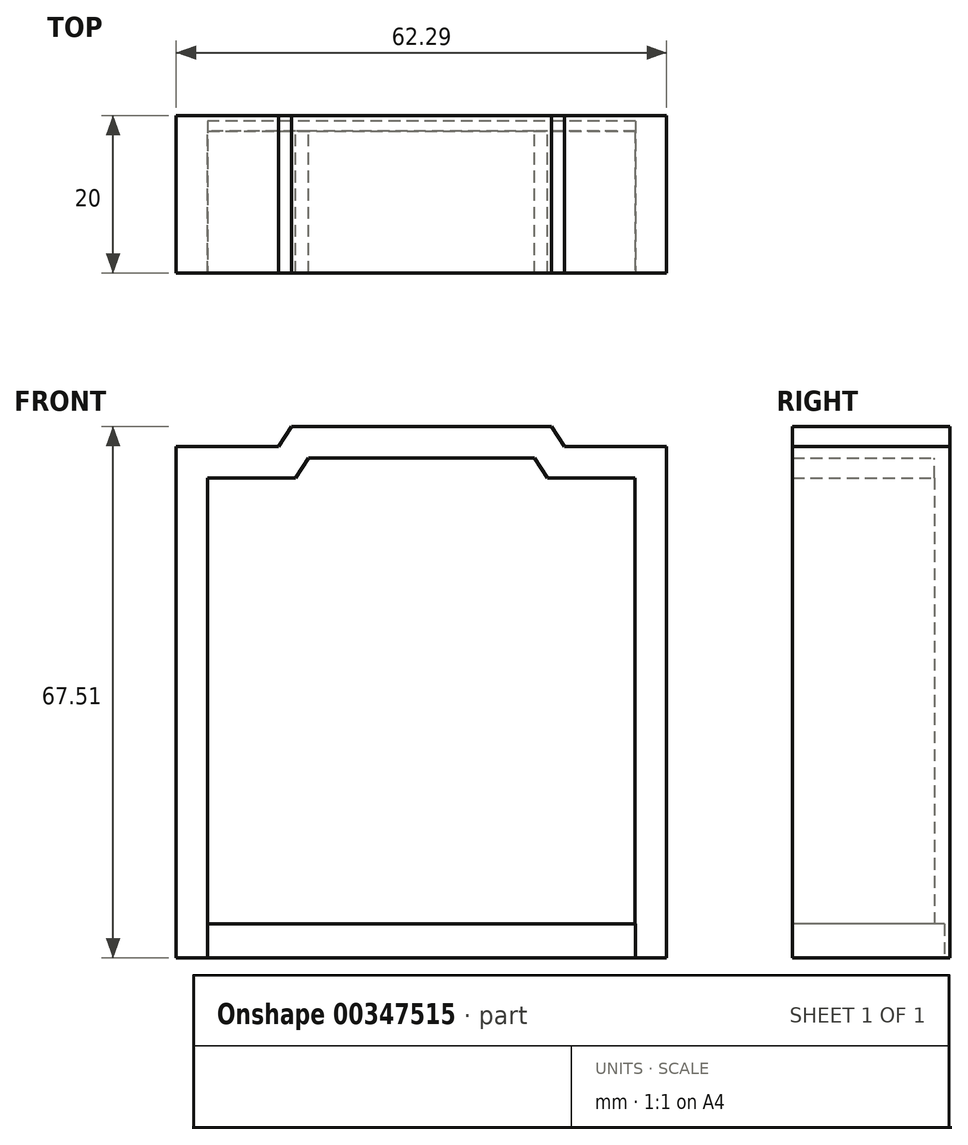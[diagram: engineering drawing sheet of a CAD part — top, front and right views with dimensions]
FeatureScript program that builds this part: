
annotation { "Feature Type Name" : "Feature", "Feature Type Description" : "" }
export const myFeature = defineFeature(function(context is Context, id is Id, definition is map)
    precondition{}
    {
        {
            var Q0;
            Q0=qCreatedBy(makeId("Front.planeOp"),FACE);
            var sketch = newSketch(context, id + "F0", { "sketchPlane" : qUnion([Q0])});
            skLineSegment(sketch, "E0", {"start": v(0, 0) * mm, "end": v(53, 0) * mm});
            skLineSegment(sketch, "E1", {"start": v(53, 0) * mm, "end": v(53, 65) * mm});
            skLineSegment(sketch, "E2", {"start": v(53, 65) * mm, "end": v(40, 65) * mm});
            skLineSegment(sketch, "E3", {"start": v(40, 65) * mm, "end": v(38.35, 67.5) * mm});
            skLineSegment(sketch, "E4", {"start": v(38.35, 67.5) * mm, "end": v(5.35, 67.5) * mm});
            skLineSegment(sketch, "E5", {"start": v(5.35, 67.5) * mm, "end": v(3.7, 65) * mm});
            skLineSegment(sketch, "E6", {"start": v(3.7, 65) * mm, "end": v(-9.3, 65) * mm});
            skLineSegment(sketch, "E7", {"start": v(-9.3, 65) * mm, "end": v(-9.3, 0) * mm});
            skLineSegment(sketch, "E8", {"start": v(0, 0) * mm, "end": v(-9.3, 0) * mm});
            skLineSegment(sketch, "E9.0", {"start": v(-5.3, 65) * mm, "end": v(-5.3, 0) * mm});
            skLineSegment(sketch, "E10.0", {"start": v(5.87, 61) * mm, "end": v(-9.3, 61) * mm});
            skLineSegment(sketch, "E10.1", {"start": v(7.51, 63.5) * mm, "end": v(5.87, 61) * mm});
            skLineSegment(sketch, "E10.2", {"start": v(38.35, 63.5) * mm, "end": v(7.51, 63.5) * mm});
            skLineSegment(sketch, "E11.0", {"start": v(37.84, 61) * mm, "end": v(35, 65.31) * mm});
            skLineSegment(sketch, "E11.1", {"start": v(0, 4) * mm, "end": v(-9.3, 4) * mm});
            skLineSegment(sketch, "E11.2", {"start": v(0, 4) * mm, "end": v(49, 4) * mm});
            skLineSegment(sketch, "E11.3", {"start": v(49, 4) * mm, "end": v(49, 61) * mm});
            skLineSegment(sketch, "E11.4", {"start": v(49, 61) * mm, "end": v(37.84, 61) * mm});
            skSolve(sketch);
        }
        {
            var Q0;
            Q0=makeQuery(id+"FbAIhWOmYQk6i5P_0.opExtrude","SWEPT_FACE",FACE,{"disambiguationData":[OSD([sQuery(id+"F0.wireOp",EDGE,"E0"),sQuery(id+"F0.wireOp",EDGE,"E8")])]});
            var sketch = newSketch(context, id + "F1", { "sketchPlane" : qUnion([Q0])});
            skSolve(sketch);
        }
        {
            var Q0;
            {var subQ0=sQuery(id+"F0.wireOp",EDGE,"E10.1");Q0=makeQuery(id+"F0.imprint","IMPRINT",FACE,{"disambiguationData":[TD([[makeQuery(id+"F0.imprint","IMPRINT",EDGE,{"derivedFrom":subQ0}),1.0]])]});}
            extrude(context, id + "F2", {"entities" : qUnion([Q0]), "depth" : 2 * mm});
        }
        {
            var Q0;
            Q0 = qSketchRegion(id + "F1", true);
            var Q1;
            Q1 = qSketchRegion(id + "F0", true);
            extrude(context, id + "F3", {"entities" : qUnion([Q0, Q1]), "operationType" : NewBodyOperationType.ADD, "depth" : 20 * mm});
        }
        {
            var Q0;
            Q0=makeQuery(id+"F3.opExtrude","SWEPT_FACE",FACE,{"disambiguationData":[OSD([sQuery(id+"F0.wireOp",EDGE,"E0"),sQuery(id+"F0.wireOp",EDGE,"E8")])]});
            extrude(context, id + "F4", {"entities" : qUnion([Q0]), "operationType" : NewBodyOperationType.ADD, "oppositeDirection" : true, "depth" : 4.3 * mm});
        }
        {
            var Q0;
            Q0=makeQuery(id+"F3.opExtrude","SWEPT_FACE",FACE,{"disambiguationData":[OSD([sQuery(id+"F0.wireOp",EDGE,"E0"),sQuery(id+"F0.wireOp",EDGE,"E8")])]});
            extrude(context, id + "F5", {"entities" : qUnion([Q0]), "operationType" : NewBodyOperationType.ADD, "oppositeDirection" : true, "depth" : 4 * mm});
        }
        {
            var Q0;
            {var subQ0=sQuery(id+"F0.wireOp",EDGE,"E8");var subQ1=sQuery(id+"F0.wireOp",EDGE,"E0");Q0=makeQuery(id+"F4.boolean.opBoolean","MERGE",FACE,{"derivedFrom":[makeQuery(id+"F3.opExtrude","CAP_FACE",FACE,{"disambiguationData":[OSD([subQ1,sQuery(id+"F0.wireOp",EDGE,"E1"),sQuery(id+"F0.wireOp",EDGE,"E2"),sQuery(id+"F0.wireOp",EDGE,"E3"),sQuery(id+"F0.wireOp",EDGE,"E4"),sQuery(id+"F0.wireOp",EDGE,"E5"),sQuery(id+"F0.wireOp",EDGE,"E6"),sQuery(id+"F0.wireOp",EDGE,"E7"),subQ0,sQuery(id+"F0.wireOp",EDGE,"E9.0"),sQuery(id+"F0.wireOp",EDGE,"E10.0"),sQuery(id+"F0.wireOp",EDGE,"E10.1"),sQuery(id+"F0.wireOp",EDGE,"E10.2"),sQuery(id+"F0.wireOp",EDGE,"E11.0"),sQuery(id+"F0.wireOp",EDGE,"E11.1"),sQuery(id+"F0.wireOp",EDGE,"E11.2"),sQuery(id+"F0.wireOp",EDGE,"E11.3"),sQuery(id+"F0.wireOp",EDGE,"E11.4")])],"isStart":false}),makeQuery(id+"F4.opExtrude","SWEPT_FACE",FACE,{"disambiguationData":[OSD([subQ1,subQ0]),TDD([makeQuery(id+"F3.opExtrude","CAP_EDGE",EDGE,{"disambiguationData":[OSD([subQ1,subQ0])],"isStart":false})])]})]});}
            var sketch = newSketch(context, id + "F6", { "sketchPlane" : qUnion([Q0])});
            skLineSegment(sketch, "E12.bottom", {"start": v(-5.3, 4.3) * mm, "end": v(49.08, 4.3) * mm});
            skLineSegment(sketch, "E12.top", {"start": v(-5.3, 0) * mm, "end": v(49.08, 0) * mm});
            skLineSegment(sketch, "E12.left", {"start": v(-5.3, 4.3) * mm, "end": v(-5.3, 0) * mm});
            skLineSegment(sketch, "E12.right", {"start": v(49.08, 4.3) * mm, "end": v(49.08, 0) * mm});
            skSolve(sketch);
        }
        {
            var Q0;
            Q0=makeQuery(id+"F6.imprint","IMPRINT",FACE,{"disambiguationData":[TD([[makeQuery(id+"F6.imprint","IMPRINT",EDGE,{"derivedFrom":sQuery(id+"F6.wireOp",EDGE,"E12.top")}),-1.0]])]});
            extrude(context, id + "F7", {"entities" : qUnion([Q0]), "operationType" : NewBodyOperationType.REMOVE, "oppositeDirection" : true, "depth" : 19.3 * mm});
        }
    });
